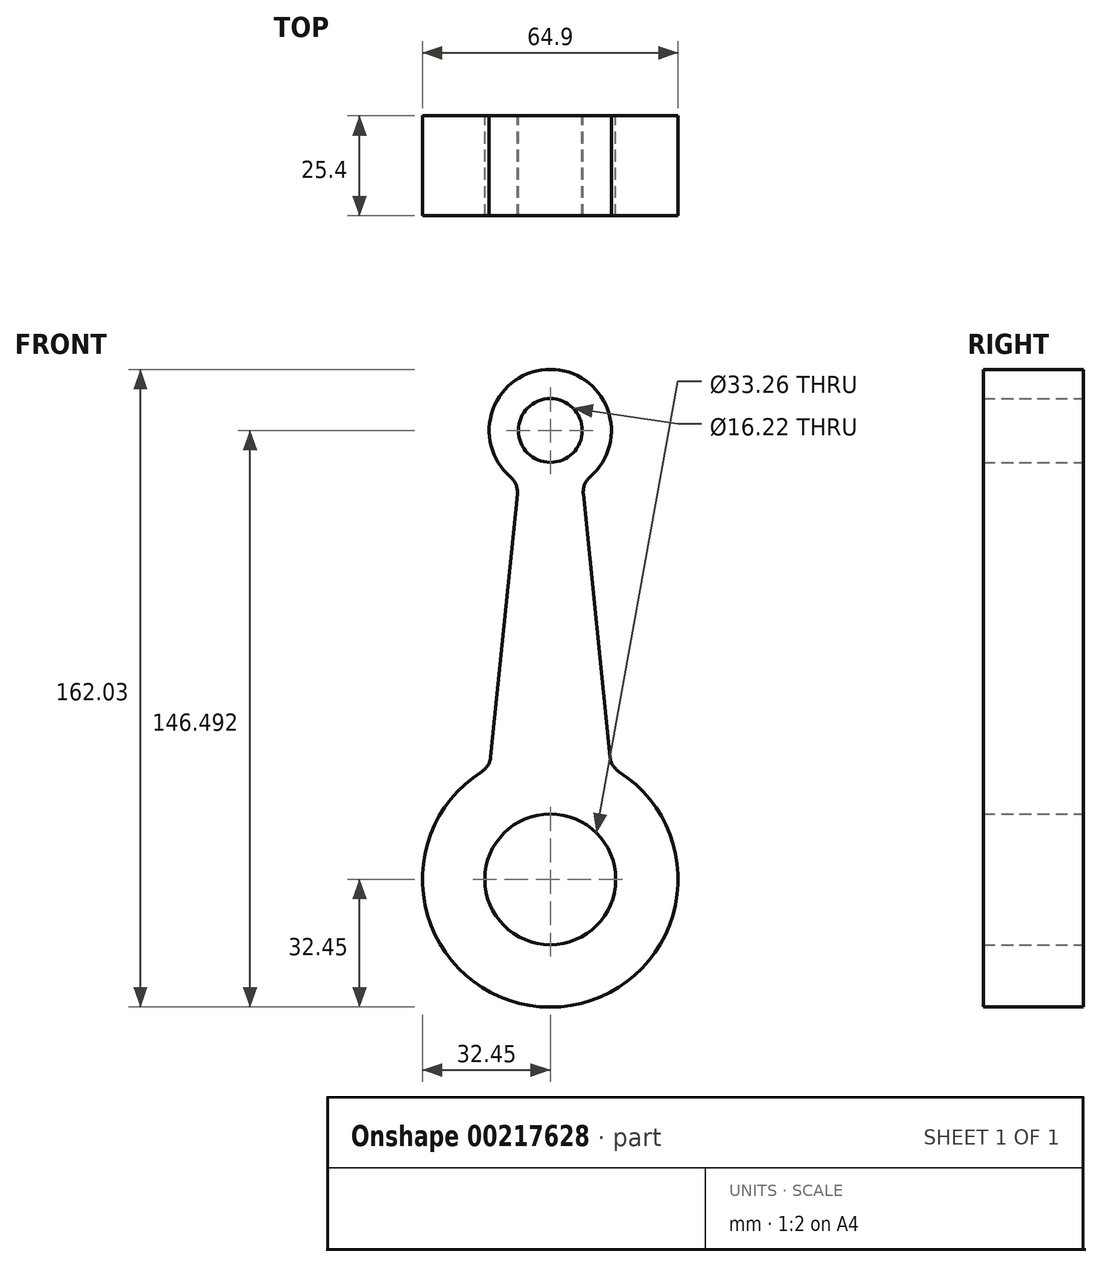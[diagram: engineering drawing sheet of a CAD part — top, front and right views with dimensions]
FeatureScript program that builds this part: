
annotation { "Feature Type Name" : "Feature", "Feature Type Description" : "" }
export const myFeature = defineFeature(function(context is Context, id is Id, definition is map)
    precondition{}
    {
        {
            var Q0;
            Q0=qCreatedBy(makeId("Front.planeOp"),FACE);
            var sketch = newSketch(context, id + "F0", { "sketchPlane" : qUnion([Q0])});
            skCircle(sketch, "E0", {"center": v(0, 0) * mm, "radius": 16.63 * mm});
            skCircle(sketch, "E1", {"center": v(0, 0) * mm, "radius": 32.45 * mm});
            skCircle(sketch, "E2", {"center": v(0, 114.04) * mm, "radius": 15.54 * mm});
            skCircle(sketch, "E3", {"center": v(0, 114.04) * mm, "radius": 8.11 * mm});
            skLineSegment(sketch, "E4", {"start": v(-8.1, 100.78) * mm, "end": v(-15.41, 28.56) * mm});
            skLineSegment(sketch, "E5", {"start": v(8.1, 100.78) * mm, "end": v(15.41, 28.56) * mm});
            skSolve(sketch);
        }
        {
            var Q0;
            Q0 = qSketchRegion(id + "F0", true);
            extrude(context, id + "F1", {"entities" : qUnion([Q0]), "depth" : 25.4 * mm});
        }
        {
            var Q0;
            Q0=makeQuery(id+"F1.opExtrude","SWEPT_EDGE",EDGE,{"disambiguationData":[OSD([sQuery(id+"F0.wireOp",EDGE,"E1"),sQuery(id+"F0.wireOp",EDGE,"E5")])]});
            var Q1;
            Q1=makeQuery(id+"F1.opExtrude","SWEPT_EDGE",EDGE,{"disambiguationData":[OSD([sQuery(id+"F0.wireOp",EDGE,"E1"),sQuery(id+"F0.wireOp",EDGE,"E4")])]});
            var Q2;
            Q2=makeQuery(id+"F1.opExtrude","SWEPT_EDGE",EDGE,{"disambiguationData":[OSD([sQuery(id+"F0.wireOp",EDGE,"E2"),sQuery(id+"F0.wireOp",EDGE,"E4")])]});
            var Q3;
            Q3=makeQuery(id+"F1.opExtrude","SWEPT_EDGE",EDGE,{"disambiguationData":[OSD([sQuery(id+"F0.wireOp",EDGE,"E2"),sQuery(id+"F0.wireOp",EDGE,"E5")])]});
            fillet(context, id + "F2", {"entities" : qUnion([Q0, Q1, Q2, Q3]), "radius" : 5.08 * mm, "tangentPropagation" : true, "allowEdgeOverflow" : false});
        }
    });
